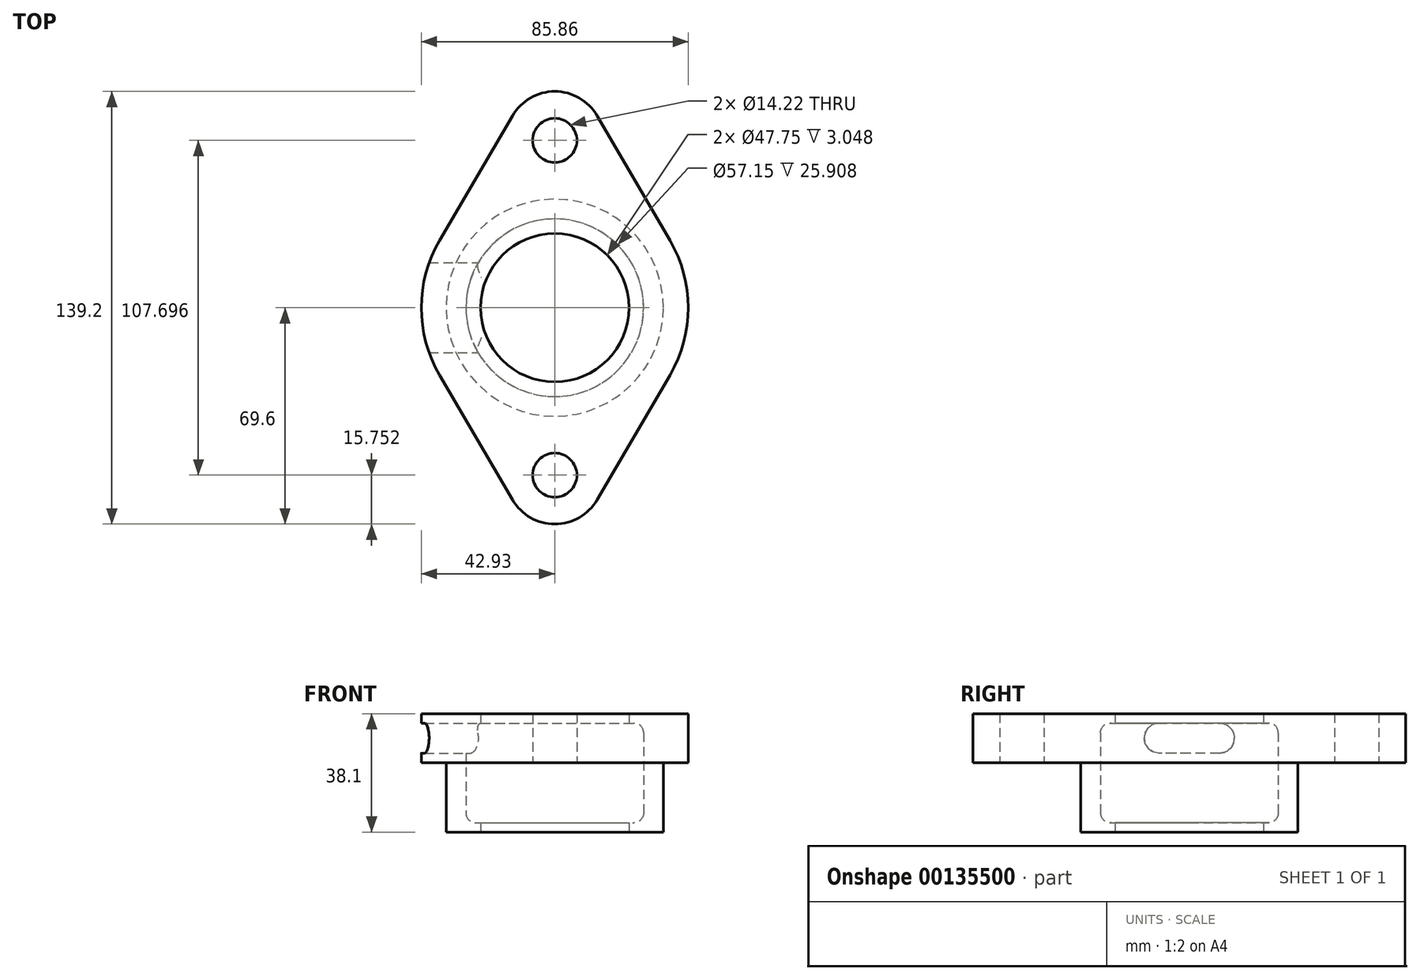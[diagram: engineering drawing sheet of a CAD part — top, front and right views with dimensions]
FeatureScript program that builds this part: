
annotation { "Feature Type Name" : "Feature", "Feature Type Description" : "" }
export const myFeature = defineFeature(function(context is Context, id is Id, definition is map)
    precondition{}
    {
        {
            var Q0;
            Q0=qCreatedBy(makeId("Top.planeOp"),FACE);
            var sketch = newSketch(context, id + "F0", { "sketchPlane" : qUnion([Q0])});
            skCircle(sketch, "E0", {"center": v(0, 0) * mm, "radius": 23.88 * mm});
            skCircle(sketch, "E1", {"center": v(0, 0) * mm, "radius": 34.93 * mm});
            skCircle(sketch, "E2", {"center": v(0, 0) * mm, "radius": 28.58 * mm, "construction": true});
            skLineSegment(sketch, "E3", {"start": v(-37.06, 21.67) * mm, "end": v(-13.6, 61.8) * mm});
            skLineSegment(sketch, "E4", {"start": v(13.6, 61.8) * mm, "end": v(37.06, 21.67) * mm});
            skLineSegment(sketch, "E5", {"start": v(13.6, -61.8) * mm, "end": v(37.06, -21.67) * mm});
            skLineSegment(sketch, "E6", {"start": v(-37.06, -21.67) * mm, "end": v(-13.6, -61.8) * mm});
            skArc(sketch, "E7", {"start": v(13.6, 61.8) * mm, "mid": v(0, 69.6) * mm, "end": v(-13.6, 61.8) * mm});
            skArc(sketch, "E8", {"start": v(-37.06, 21.67) * mm, "mid": v(-42.93, 0) * mm, "end": v(-37.06, -21.67) * mm});
            skArc(sketch, "E9", {"start": v(37.06, -21.67) * mm, "mid": v(42.93, 0) * mm, "end": v(37.06, 21.67) * mm});
            skArc(sketch, "E10", {"start": v(-13.6, -61.8) * mm, "mid": v(0, -69.6) * mm, "end": v(13.6, -61.8) * mm});
            skCircle(sketch, "E11", {"center": v(0, 53.85) * mm, "radius": 7.11 * mm});
            skCircle(sketch, "E12", {"center": v(0, -53.85) * mm, "radius": 7.11 * mm});
            skSolve(sketch);
        }
        {
            var Q0;
            Q0=makeQuery(id+"F0.imprint","IMPRINT",FACE,{"disambiguationData":[TD([[makeQuery(id+"F0.imprint","IMPRINT",EDGE,{"derivedFrom":sQuery(id+"F0.wireOp",EDGE,"E1")}),-1.0]])]});
            var Q1;
            Q1=makeQuery(id+"F0.imprint","IMPRINT",FACE,{"disambiguationData":[TD([[makeQuery(id+"F0.imprint","IMPRINT",EDGE,{"derivedFrom":sQuery(id+"F0.wireOp",EDGE,"E0")}),-1.0]])]});
            var Q2;
            Q2=makeQuery(id+"F0.imprint","IMPRINT",FACE,{"disambiguationData":[TD([[makeQuery(id+"F0.imprint","IMPRINT",EDGE,{"derivedFrom":sQuery(id+"F0.wireOp",EDGE,"E0")}),1.0]])]});
            extrude(context, id + "F1", {"entities" : qUnion([Q0, Q1, Q2]), "depth" : 15.75 * mm});
        }
        {
            var Q0;
            Q0=makeQuery(id+"F1.opExtrude","CAP_FACE",FACE,{"disambiguationData":[OSD([sQuery(id+"F0.wireOp",EDGE,"E3"),sQuery(id+"F0.wireOp",EDGE,"E4"),sQuery(id+"F0.wireOp",EDGE,"E5"),sQuery(id+"F0.wireOp",EDGE,"E6"),sQuery(id+"F0.wireOp",EDGE,"E7"),sQuery(id+"F0.wireOp",EDGE,"E8"),sQuery(id+"F0.wireOp",EDGE,"E9"),sQuery(id+"F0.wireOp",EDGE,"E10"),sQuery(id+"F0.wireOp",EDGE,"E11"),sQuery(id+"F0.wireOp",EDGE,"E12")])],"isStart":true});
            var sketch = newSketch(context, id + "F2", { "sketchPlane" : qUnion([Q0])});
            skCircle(sketch, "E13", {"center": v(0, 0) * mm, "radius": 34.93 * mm});
            skSolve(sketch);
        }
        {
            var Q0;
            Q0 = qSketchRegion(id + "F2", true);
            extrude(context, id + "F3", {"entities" : qUnion([Q0]), "operationType" : NewBodyOperationType.ADD, "depth" : 22.35 * mm});
        }
        {
            var Q0;
            Q0=qCreatedBy(makeId("Front.planeOp"),FACE);
            var sketch = newSketch(context, id + "F4", { "sketchPlane" : qUnion([Q0])});
            skLineSegment(sketch, "E14", {"start": v(0, 15.75) * mm, "end": v(0, -22.35) * mm});
            skLineSegment(sketch, "E15", {"start": v(0, 15.75) * mm, "end": v(-23.88, 15.75) * mm});
            skLineSegment(sketch, "E16", {"start": v(-23.88, 15.75) * mm, "end": v(-23.88, 12.7) * mm});
            skLineSegment(sketch, "E17", {"start": v(-23.88, 12.7) * mm, "end": v(-25.53, 12.7) * mm});
            skLineSegment(sketch, "E18", {"start": v(-28.58, 9.65) * mm, "end": v(-28.57, -16.26) * mm});
            skLineSegment(sketch, "E19", {"start": v(-25.53, -19.3) * mm, "end": v(-23.88, -19.3) * mm});
            skLineSegment(sketch, "E20", {"start": v(-23.88, -19.3) * mm, "end": v(-23.88, -22.35) * mm});
            skLineSegment(sketch, "E21", {"start": v(-23.88, -22.35) * mm, "end": v(0, -22.35) * mm});
            skPoint(sketch, "E22.visualSharp", {"position": v(-28.58, 12.7) * mm});
            skArc(sketch, "E22.filletArc", {"start": v(-25.53, 12.7) * mm, "mid": v(-27.68, 11.8) * mm, "end": v(-28.58, 9.65) * mm});
            skPoint(sketch, "E23.visualSharp", {"position": v(-28.57, -19.3) * mm});
            skArc(sketch, "E23.filletArc", {"start": v(-28.57, -16.26) * mm, "mid": v(-27.68, -18.41) * mm, "end": v(-25.53, -19.3) * mm});
            skSolve(sketch);
        }
        {
            var Q0;
            Q0 = qSketchRegion(id + "F4", true);
            var Q1;
            Q1=sQuery(id+"F4.wireOp",EDGE,"E14");
            revolve(context, id + "F5", {"operationType" : NewBodyOperationType.REMOVE, "entities" : qUnion([Q0]), "axis" : qUnion([Q1]), "revolveType" : RevolveType.FULL, "oppositeDirection" : true});
        }
        {
            var Q0;
            Q0=qCreatedBy(makeId("Right.planeOp"),FACE);
            var sketch = newSketch(context, id + "F6", { "sketchPlane" : qUnion([Q0])});
            skLineSegment(sketch, "E24", {"start": v(9.65, 7.87) * mm, "end": v(-9.65, 7.87) * mm, "construction": true});
            skArc(sketch, "E25.0.startCap", {"start": v(9.65, 12.7) * mm, "mid": v(14.48, 7.87) * mm, "end": v(9.65, 3.05) * mm});
            skArc(sketch, "E25.0.endCap", {"start": v(-9.65, 3.05) * mm, "mid": v(-14.48, 7.87) * mm, "end": v(-9.65, 12.7) * mm});
            skLineSegment(sketch, "E25.0.left", {"start": v(9.65, 3.05) * mm, "end": v(-9.65, 3.05) * mm});
            skLineSegment(sketch, "E25.0.right", {"start": v(9.65, 12.7) * mm, "end": v(-9.65, 12.7) * mm});
            skSolve(sketch);
        }
        {
            var Q0;
            Q0 = qSketchRegion(id + "F6", true);
            var Q1;
            Q1=makeQuery(id+"F1.opExtrude","SWEPT_FACE",FACE,{"disambiguationData":[OSD([sQuery(id+"F0.wireOp",EDGE,"E8")])]});
            extrude(context, id + "F7", {"entities" : qUnion([Q0]), "operationType" : NewBodyOperationType.REMOVE, "endBound" : BoundingType.UP_TO_SURFACE, "oppositeDirection" : true, "endBoundEntityFace" : qUnion([Q1]), "depth" : 25.4 * mm});
        }
    });
